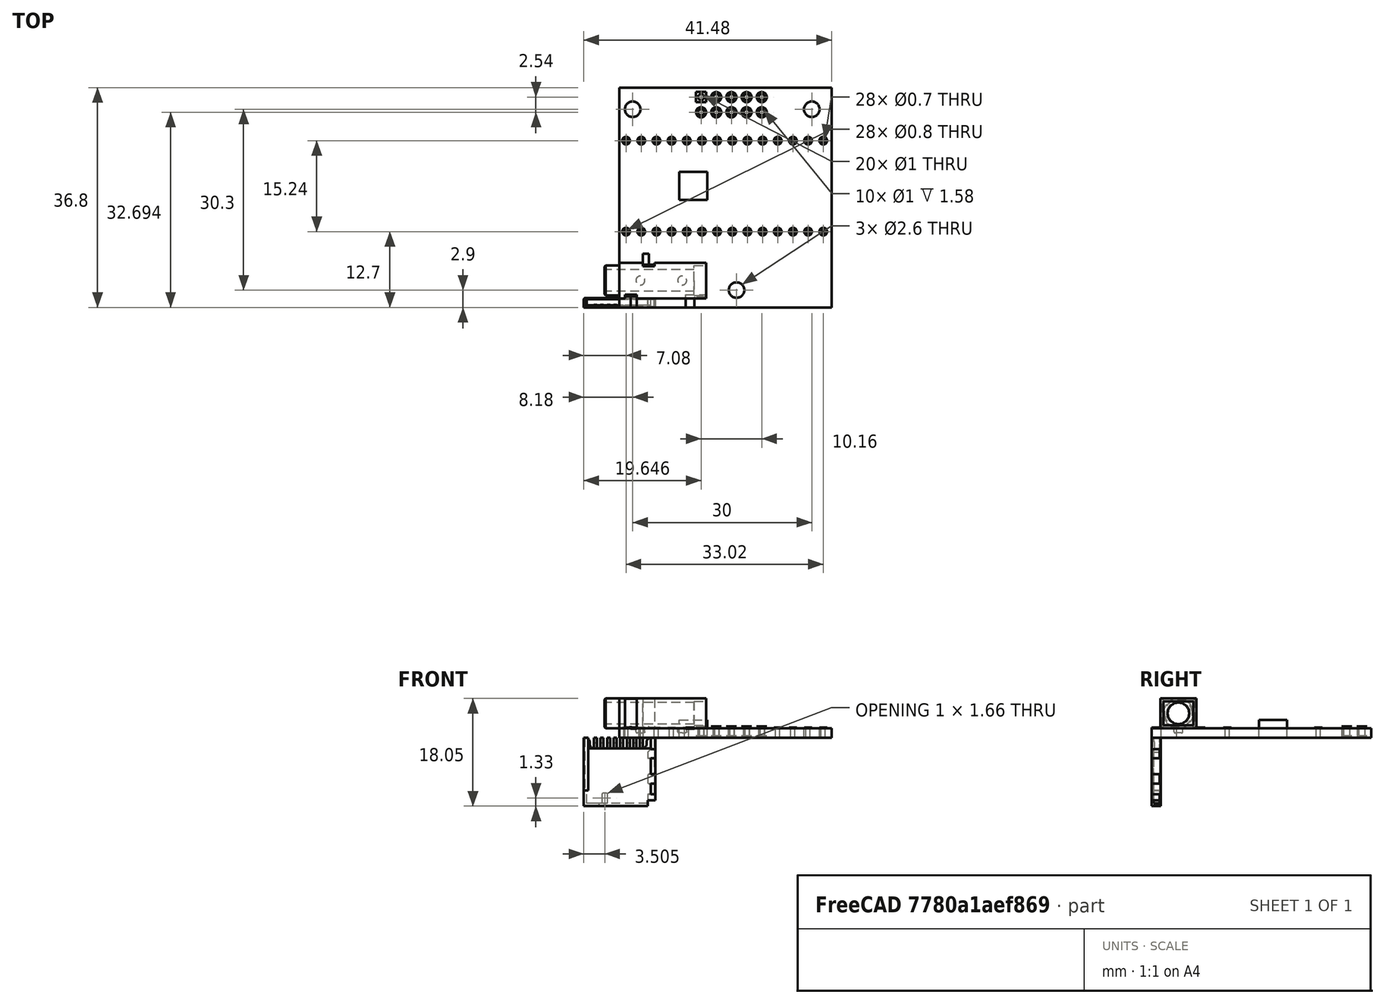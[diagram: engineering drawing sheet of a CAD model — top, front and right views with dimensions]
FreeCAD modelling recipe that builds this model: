
FCSTD DOCUMENT  (FreeCAD 0.18.4R)
Label: TeensyAudioBoard good without extra sdcard and 2x5 pins
License: All rights reserved
LicenseURL: http://en.wikipedia.org/wiki/All_rights_reserved
objects: Part::Cylinder×19, Part::Cut×19, Part::Feature×11, PartDesign::Body×8, Part::Compound×4, Part::FeaturePython×3, Part::Box×2, App::Part×2, Part::Part2DObjectPython×2, App::DocumentObjectGroup×2
note: 68 computed .brp shape members not serialized (recipe doc carries the construction recipe); baked Part::Feature solids carry a one-line shape summary decoded from their .brp

FEATURE [Part::Feature] Part__Feature  label="CUI_DEVICES_SJ-3523-SMT-TR"
  Placement = pos=(0,4.5,1.6) rot=(1,0,0;1.5708rad)
  shape: bbox 17 x 9 x 5.8 mm, 69 faces (baked)
FEATURE [Part::Box] Box  label="Cube"
  AttacherType = Attacher::AttachEngine3D
  Height = 1.6
  Length = 35.5
  Width = 36.8
FEATURE [Part::Cylinder] Cylinder
  Angle = 360
  AttacherType = Attacher::AttachEngine3D
  Height = 1.6
  Placement = pos=(19.6,2.9,0) rot=(0,0,1;0rad)
  Radius = 1.3
FEATURE [Part::Cut] Cut
  Base = -> Box
  Tool = -> Cylinder
FEATURE [Part::Cylinder] Cylinder001
  Angle = 360
  AttacherType = Attacher::AttachEngine3D
  Height = 1.6
  Placement = pos=(2.2,33.2,0) rot=(0,0,1;0rad)
  Radius = 1.3
FEATURE [Part::Cut] Cut001
  Base = -> Cut
  Tool = -> Cylinder001
FEATURE [Part::Cylinder] Cylinder002
  Angle = 360
  AttacherType = Attacher::AttachEngine3D
  Height = 1.6
  Placement = pos=(32.2,33.2,0) rot=(0,0,1;0rad)
  Radius = 1.3
FEATURE [Part::Cut] Cut002
  Base = -> Cut001
  Tool = -> Cylinder002
FEATURE [Part::Feature] Part__Feature043  label="Component047"
  shape: bbox 0.5 x 0.45 x 1.8 mm, 8 faces (baked)
FEATURE [Part::Feature] Part__Feature044  label="Component048"
  Placement = pos=(4.4,0,9e-15) rot=(0,0,1;0rad)
  shape: bbox 0.5 x 0.45 x 1.8 mm, 8 faces (baked)
FEATURE [Part::Feature] Part__Feature046  label="Component050"
  Placement = pos=(5.5,0,9e-15) rot=(0,0,1;0rad)
  shape: bbox 0.5 x 0.45 x 1.8 mm, 8 faces (baked)
FEATURE [Part::Feature] Part__Feature045  label="Component049"
  Placement = pos=(1.1,0,0) rot=(0,0,1;0rad)
  shape: bbox 0.5 x 0.45 x 1.8 mm, 8 faces (baked)
FEATURE [Part::Feature] Part__Feature047  label="Component051"
  Placement = pos=(6.6,0,0) rot=(0,0,1;0rad)
  shape: bbox 0.5 x 0.45 x 1.8 mm, 8 faces (baked)
FEATURE [Part::Feature] Part__Feature048  label="Component052"
  Placement = pos=(3.3,0,0) rot=(0,0,1;0rad)
  shape: bbox 0.5 x 0.45 x 1.8 mm, 8 faces (baked)
FEATURE [Part::Feature] Part__Feature049  label="Component053"
  Placement = pos=(2.2,0,0) rot=(0,0,1;0rad)
  shape: bbox 0.5 x 0.45 x 1.8 mm, 8 faces (baked)
FEATURE [Part::Feature] Part__Feature050  label="Case"
  shape: bbox 11.95 x 1.55 x 11.45 mm, 59 faces (baked)
FEATURE [App::Part] Pins
  Origin = -> Origin006
FEATURE [Part::Feature] Part__Feature041  label="Base"
  shape: bbox 11.95 x 1.35 x 9.65 mm, 32 faces (baked)
FEATURE [Part::Feature] Part__Feature042  label="Component2"
  Placement = pos=(7.7,0,0) rot=(0,0,1;0rad)
  shape: bbox 0.5 x 0.45 x 1.8 mm, 8 faces (baked)
FEATURE [PartDesign::Body] Body
  Origin = -> Origin
FEATURE [PartDesign::Body] Body001
  Origin = -> Origin008
FEATURE [PartDesign::Body] Body002
  Origin = -> Origin009
FEATURE [PartDesign::Body] Body003
  Origin = -> Origin010
FEATURE [PartDesign::Body] Body004
  Origin = -> Origin011
FEATURE [PartDesign::Body] Body005
  Origin = -> Origin012
FEATURE [PartDesign::Body] Body006
  Origin = -> Origin013
FEATURE [PartDesign::Body] Body007
  Origin = -> Origin014
FEATURE [App::Part] HR5_DM3D_Micro_SD_Card_v4  label="SD card"
  Group = -> [Part__Feature041,Pins,Part__Feature050,Body,Body001,Body002,Body003,Body004,Body005,Body006,Body007,Part__Feature042,Part__Feature043,Part__Feature044,Part__Feature045,Part__Feature046,Part__Feature047,Part__Feature048,Part__Feature049]
  Origin = -> Origin007
  Placement = pos=(35.5,20.5,1.6) rot=(0.57735,0.57735,0.57735;2.0944rad)
FEATURE [Part::Cylinder] Cylinder004
  Angle = 360
  AttacherType = Attacher::AttachEngine3D
  Height = 1.6
  Placement = pos=(3.64,12.7,0) rot=(0,0,1;0rad)
  Radius = 0.35
FEATURE [Part::Cylinder] Cylinder008
  Angle = 360
  AttacherType = Attacher::AttachEngine3D
  Height = 1.6
  Placement = pos=(1.1,12.7,0) rot=(0,0,1;0rad)
  Radius = 0.35
FEATURE [Part::Cylinder] Cylinder009
  Angle = 360
  AttacherType = Attacher::AttachEngine3D
  Height = 1.6
  Placement = pos=(8.72,12.7,0) rot=(0,0,1;0rad)
  Radius = 0.35
FEATURE [Part::Cylinder] Cylinder010
  Angle = 360
  AttacherType = Attacher::AttachEngine3D
  Height = 1.6
  Placement = pos=(6.18,12.7,0) rot=(0,0,1;0rad)
  Radius = 0.35
FEATURE [Part::Cylinder] Cylinder011
  Angle = 360
  AttacherType = Attacher::AttachEngine3D
  Height = 1.6
  Placement = pos=(11.26,12.7,0) rot=(0,0,1;0rad)
  Radius = 0.35
FEATURE [Part::Cylinder] Cylinder012
  Angle = 360
  AttacherType = Attacher::AttachEngine3D
  Height = 1.6
  Placement = pos=(13.8,12.7,0) rot=(0,0,1;0rad)
  Radius = 0.35
FEATURE [Part::Cylinder] Cylinder013
  Angle = 360
  AttacherType = Attacher::AttachEngine3D
  Height = 1.6
  Placement = pos=(18.88,12.7,0) rot=(0,0,1;0rad)
  Radius = 0.35
FEATURE [Part::Cylinder] Cylinder014
  Angle = 360
  AttacherType = Attacher::AttachEngine3D
  Height = 1.6
  Placement = pos=(23.96,12.7,0) rot=(0,0,1;0rad)
  Radius = 0.35
FEATURE [Part::Cylinder] Cylinder015
  Angle = 360
  AttacherType = Attacher::AttachEngine3D
  Height = 1.6
  Placement = pos=(21.42,12.7,0) rot=(0,0,1;0rad)
  Radius = 0.35
FEATURE [Part::Cylinder] Cylinder016
  Angle = 360
  AttacherType = Attacher::AttachEngine3D
  Height = 1.6
  Placement = pos=(16.34,12.7,0) rot=(0,0,1;0rad)
  Radius = 0.35
FEATURE [Part::Cylinder] Cylinder017
  Angle = 360
  AttacherType = Attacher::AttachEngine3D
  Height = 1.6
  Placement = pos=(29.04,12.7,0) rot=(0,0,1;0rad)
  Radius = 0.35
FEATURE [Part::Cylinder] Cylinder018
  Angle = 360
  AttacherType = Attacher::AttachEngine3D
  Height = 1.6
  Placement = pos=(34.12,12.7,0) rot=(0,0,1;0rad)
  Radius = 0.35
FEATURE [Part::Cylinder] Cylinder019
  Angle = 360
  AttacherType = Attacher::AttachEngine3D
  Height = 1.6
  Placement = pos=(31.58,12.7,0) rot=(0,0,1;0rad)
  Radius = 0.35
FEATURE [Part::Cylinder] Cylinder020
  Angle = 360
  AttacherType = Attacher::AttachEngine3D
  Height = 1.6
  Placement = pos=(26.5,12.7,0) rot=(0,0,1;0rad)
  Radius = 0.35
FEATURE [Part::Compound] Compound
  Links = -> [Cylinder004,Cylinder008,Cylinder009,Cylinder013,Cylinder018,Cylinder012,Cylinder015,Cylinder014,Cylinder016,Cylinder011,Cylinder010,Cylinder019,Cylinder020,Cylinder017]
FEATURE [Part::Compound] Compound001
  Links = -> [Cylinder004,Cylinder008,Cylinder009,Cylinder013,Cylinder018,Cylinder012,Cylinder015,Cylinder014,Cylinder016,Cylinder011,Cylinder010,Cylinder019,Cylinder020,Cylinder017]
  Placement = pos=(0,15.24,0) rot=(0,0,1;0rad)
FEATURE [Part::Cut] Cut004
  Base = -> Cut002
  Tool = -> Compound
FEATURE [Part::Box] Box001  label="Processor"
  AttacherType = Attacher::AttachEngine3D
  Height = 3
  Length = 4.7
  Placement = pos=(10,18,0) rot=(0,0,1;0rad)
  Width = 4.7
FEATURE [Part::Part2DObjectPython] ShapeString  label="Text board"  # Draft 2D object (typed FeaturePython)
  FontFile = <path>
  Placement = pos=(9.41606,9.04423,1.73909) rot=(0,0,1;0rad)
  Size = 2
  String = TEENSY 4 AUDIOBOARD
  Tracking = 0
FEATURE [Part::Part2DObjectPython] Line  # Draft 2D object (typed FeaturePython)
  ChamferSize = 0
  Closed = false
  End = (0.301227,8.17618,0.392706)
  FilletRadius = 0
  Length = 5
  MakeFace = false
  Placement = pos=(0.301227,13.1762,0.392706) rot=(0,0,1;0rad)
  Points = (2) [(0,0,0),(0,-5,0)]
  Start = (0.301227,13.1762,0.392706)
  Subdivisions = 0
FEATURE [Part::Cylinder] Cylinder007
  Angle = 360
  AttacherType = Attacher::AttachEngine3D
  Height = 0.1
  Placement = pos=(0,0,1.62) rot=(0,0,1;0rad)
  Radius = 0.4
FEATURE [Part::Cylinder] Cylinder006
  Angle = 360
  AttacherType = Attacher::AttachEngine3D
  Height = 0.1
  Placement = pos=(0,0,1.62) rot=(0,0,1;0rad)
  Radius = 0.65
FEATURE [Part::Cut] Cut003
  Base = -> Cylinder006
  Placement = pos=(1.1,12.7,0) rot=(0,0,1;0rad)
  Tool = -> Cylinder007
FEATURE [Part::Cut] Cut006
  Base = -> Cylinder006
  Placement = pos=(3.64,12.7,0) rot=(0,0,1;0rad)
  Tool = -> Cylinder007
FEATURE [Part::Cut] Cut008
  Base = -> Cylinder006
  Placement = pos=(8.72,12.7,0) rot=(0,0,1;0rad)
  Tool = -> Cylinder007
FEATURE [Part::Cut] Cut009
  Base = -> Cylinder006
  Placement = pos=(11.26,12.7,0) rot=(0,0,1;0rad)
  Tool = -> Cylinder007
FEATURE [Part::Cut] Cut010
  Base = -> Cylinder006
  Placement = pos=(13.8,12.7,0) rot=(0,0,1;0rad)
  Tool = -> Cylinder007
FEATURE [Part::Cut] Cut012
  Base = -> Cylinder006
  Placement = pos=(18.88,12.7,0) rot=(0,0,1;0rad)
  Tool = -> Cylinder007
FEATURE [Part::Cut] Cut013
  Base = -> Cylinder006
  Placement = pos=(21.42,12.7,0) rot=(0,0,1;0rad)
  Tool = -> Cylinder007
FEATURE [Part::Cut] Cut014
  Base = -> Cylinder006
  Placement = pos=(23.96,12.7,0) rot=(0,0,1;0rad)
  Tool = -> Cylinder007
FEATURE [Part::Cut] Cut015
  Base = -> Cylinder006
  Placement = pos=(26.5,12.7,0) rot=(0,0,1;0rad)
  Tool = -> Cylinder007
FEATURE [Part::Cut] Cut016
  Base = -> Cylinder006
  Placement = pos=(29.04,12.7,0) rot=(0,0,1;0rad)
  Tool = -> Cylinder007
FEATURE [Part::Cut] Cut017
  Base = -> Cylinder006
  Placement = pos=(31.58,12.7,0) rot=(0,0,1;0rad)
  Tool = -> Cylinder007
FEATURE [Part::Cut] Cut018
  Base = -> Cylinder006
  Placement = pos=(34.12,12.7,0) rot=(0,0,1;0rad)
  Tool = -> Cylinder007
FEATURE [Part::Cut] Cut011
  Base = -> Cylinder006
  Placement = pos=(16.34,12.7,0) rot=(0,0,1;0rad)
  Tool = -> Cylinder007
FEATURE [Part::Cut] Cut007
  Base = -> Cylinder006
  Placement = pos=(6.18,12.7,0) rot=(0,0,1;0rad)
  Tool = -> Cylinder007
FEATURE [Part::Compound] Compound002  label="Teensy pins left"
  Links = -> [Cut003,Cut006,Cut018,Cut010,Cut016,Cut013,Cut011,Cut012,Cut017,Cut008,Cut015,Cut009,Cut014,Cut007]
FEATURE [Part::Compound] Compound003  label="Teensy pins right"
  Links = -> [Cut003,Cut006,Cut018,Cut010,Cut016,Cut013,Cut011,Cut012,Cut017,Cut008,Cut015,Cut009,Cut014,Cut007]
  Placement = pos=(0,15.24,0) rot=(0,0,1;0rad)
FEATURE [Part::FeaturePython] TopPads  # a2plus imported part (geometry in sourceFile) (typed FeaturePython)
  Placement = pos=(13.6664,35.2336,1.90794) rot=(0,0,1;1.5708rad)
  fixedPosition = true
FEATURE [Part::FeaturePython] BotPads  # a2plus imported part (geometry in sourceFile) (typed FeaturePython)
  Placement = pos=(13.6664,35.2336,1.90794) rot=(0,0,1;1.5708rad)
  fixedPosition = true
FEATURE [Part::FeaturePython] THPs  label="PTHs"  # a2plus imported part (geometry in sourceFile) (typed FeaturePython)
  Placement = pos=(13.6664,35.2336,1.90794) rot=(0,0,1;1.5708rad)
  fixedPosition = true
FEATURE [App::DocumentObjectGroup] Group
FEATURE [App::DocumentObjectGroup] PinSocket_2x05_P2_54mm_Horizontal_fp  label="audio header"
  Group = -> [TopPads,BotPads,THPs,Group]
FEATURE [Part::Cut] Cut005  label="Main board"
  Base = -> Cut004
  Tool = -> Compound001
note: 1 file-system path scrubbed to <path> (originals preserved in the JSON sidecar)
